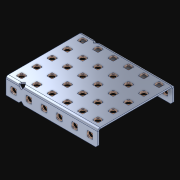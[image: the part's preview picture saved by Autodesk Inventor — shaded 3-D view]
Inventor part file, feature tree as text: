
AUTODESK INVENTOR PART (.ipt)
format: ipt  version: 2021 (Build 250183000, 183)  size: 1,519,616 bytes
history: native  units: in
note: dims shown in document units (in); Inventor stores cm internally (conversion verified against a paired STEP export)
features: extrude x43, other x43, sketch x4, pattern_linear x3
ambient origin geometry x8: Origin, YZ Plane, XZ Plane, XY Plane, X Axis, Y Axis, Z Axis, Center Point
bodies: Solid1 (feature_tree)
feature tree (93):
  pattern_linear  "Rectangular Pattern1"  Spacing1=0.182in  [1 undecoded]
  pattern_linear  "Rectangular Pattern2"  Spacing1=0.046in  [1 undecoded]
  pattern_linear  "Rectangular Pattern3"  Spacing1=0.5in  [1 undecoded]
  extrude  "Extrusion1"  Depth=0.046in
  sketch  "Sketch1"  dims[d0=0.182in]
  other  "Srf1"
  sketch  "Sketch2"  dims[d1=0.046in d2=0.0in]
  other  "Srf2"
  sketch  "Sketch3"  dims[d3=0.182in]
  other  "Srf3"
  other  "Srf4"
  other  "Srf5"
  other  "Srf6"
  other  "Srf7"
  other  "Srf8"
  other  "Srf38"
  other  "Srf39"
  other  "Srf40"
  other  "Srf41"
  other  "Srf42"
  other  "Srf72"
  other  "Srf73"
  other  "Srf74"
  other  "Srf75"
  other  "Srf76"
  other  "Srf77"
  other  "Srf107"
  other  "Srf108"
  other  "Srf109"
  other  "Srf110"
  other  "Srf111"
  other  "Srf112"
  other  "Srf142"
  other  "Srf143"
  other  "Srf144"
  other  "Srf145"
  other  "Srf146"
  other  "Srf147"
  other  "Srf177"
  other  "Srf178"
  other  "Srf179"
  other  "Srf180"
  other  "Srf181"
  other  "Srf182"
  other  "Srf212"
  other  "Srf213"
  other  "Srf214"
  other  "Srf215"
  other  "Srf216"
  sketch  "Sketch4"  dims[d4=0.046in d5=0.0in d6=0.182in d7=0.046in d8=0.0in d11=0.5in d12=2.3622in d14=0.5in d15=1.9685in d17=0.5in d18=2.3622in d20=0.5in d21=14.5in d22=0.0in]
  parser-record x1  (decoder bookkeeping rows leaked as tree rows — omitted from the tree; the rows remain in map.json)
  extrude  "ExtrusionSrf1"  Depth=0.046in
  extrude  "ExtrusionSrf2"  Depth=0.046in
  extrude  "ExtrusionSrf3"  Depth=0.046in
  extrude  "ExtrusionSrf4"  Depth=0.046in
  extrude  "ExtrusionSrf5"  Depth=0.046in
  extrude  "ExtrusionSrf6"  TaperAngle=0.0deg  [1 undecoded]
  extrude  "ExtrusionSrf7"  [1 undecoded]
  extrude  "ExtrusionSrf8"  [1 undecoded]
  extrude  "ExtrusionSrf38"  [1 undecoded]
  extrude  "ExtrusionSrf39"  [1 undecoded]
  extrude  "ExtrusionSrf40"  [1 undecoded]
  extrude  "ExtrusionSrf41"  [1 undecoded]
  extrude  "ExtrusionSrf42"  [1 undecoded]
  extrude  "ExtrusionSrf72"  [1 undecoded]
  extrude  "ExtrusionSrf73"  [1 undecoded]
  extrude  "ExtrusionSrf74"  [1 undecoded]
  extrude  "ExtrusionSrf75"  [1 undecoded]
  extrude  "ExtrusionSrf76"  [1 undecoded]
  extrude  "ExtrusionSrf77"  [1 undecoded]
  extrude  "ExtrusionSrf107"  [1 undecoded]
  extrude  "ExtrusionSrf108"  [1 undecoded]
  extrude  "ExtrusionSrf109"  [1 undecoded]
  extrude  "ExtrusionSrf110"  [1 undecoded]
  extrude  "ExtrusionSrf111"  [1 undecoded]
  extrude  "ExtrusionSrf112"  [1 undecoded]
  extrude  "ExtrusionSrf142"  [1 undecoded]
  extrude  "ExtrusionSrf143"  [1 undecoded]
  extrude  "ExtrusionSrf144"  [1 undecoded]
  extrude  "ExtrusionSrf145"  [1 undecoded]
  extrude  "ExtrusionSrf146"  [1 undecoded]
  extrude  "ExtrusionSrf147"  [1 undecoded]
  extrude  "ExtrusionSrf177"  [1 undecoded]
  extrude  "ExtrusionSrf178"  [1 undecoded]
  extrude  "ExtrusionSrf179"  [1 undecoded]
  extrude  "ExtrusionSrf180"  [1 undecoded]
  extrude  "ExtrusionSrf181"  [1 undecoded]
  extrude  "ExtrusionSrf182"  [1 undecoded]
  extrude  "ExtrusionSrf212"  [1 undecoded]
  extrude  "ExtrusionSrf213"  [1 undecoded]
  extrude  "ExtrusionSrf214"  [1 undecoded]
  extrude  "ExtrusionSrf215"  [1 undecoded]
  extrude  "ExtrusionSrf216"  [1 undecoded]
note: 40 required parameter values undecoded (feature->parameter linkage not recoverable at this tier; creation-order binding heuristic only, values carry confidence <= 0.55)
